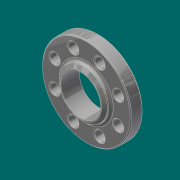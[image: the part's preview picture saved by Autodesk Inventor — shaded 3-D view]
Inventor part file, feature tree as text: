
AUTODESK INVENTOR PART (.ipt)
format: ipt  version: 2017.3 (Build 213257000, 257)  size: 250,880 bytes
history: native  units: in
note: dims shown in document units (in); Inventor stores cm internally (conversion verified against a paired STEP export)
features: chamfer x2, sketch x2, revolve x1, hole x1, pattern_circular x1
ambient origin geometry x8: Origin, YZ Plane, XZ Plane, XY Plane, X Axis, Y Axis, Z Axis, Center Point
bodies: Solid1 (feature_tree)
feature tree (7):
  revolve  "Revolution1"  [1 undecoded]
  hole  "Hole1"  [1 undecoded]
  chamfer  "Chamfer1"  Distance=0.0625in
  pattern_circular  "Circular Pattern1"  [2 undecoded]
  chamfer  "Chamfer2"  Distance=2.9in
  sketch  "Sketch1"  dims[d0=1.3438in d1=6.5in]
  sketch  "Sketch2"  dims[d2=0.9375in d3=3.625in d4=0.0625in d5=3.5in d6=2.9in d7=3.61in d8=0.2577in d9=0.2375in d10=0.2in d11=90.0deg d12=5.0in d13=22.5deg d14=0.75in d15=0.75in d16=0.375in d17=0.25in d18=0.5635in d19=1.0in d20=0.8108in d21=0.0469in d22=0.125in d23=45.0deg d24=3.1496in d25=360.0deg d27=0.0625in d28=0.125in d29=45.0deg]
note: 4 required parameter values undecoded (feature->parameter linkage not recoverable at this tier; creation-order binding heuristic only, values carry confidence <= 0.55)